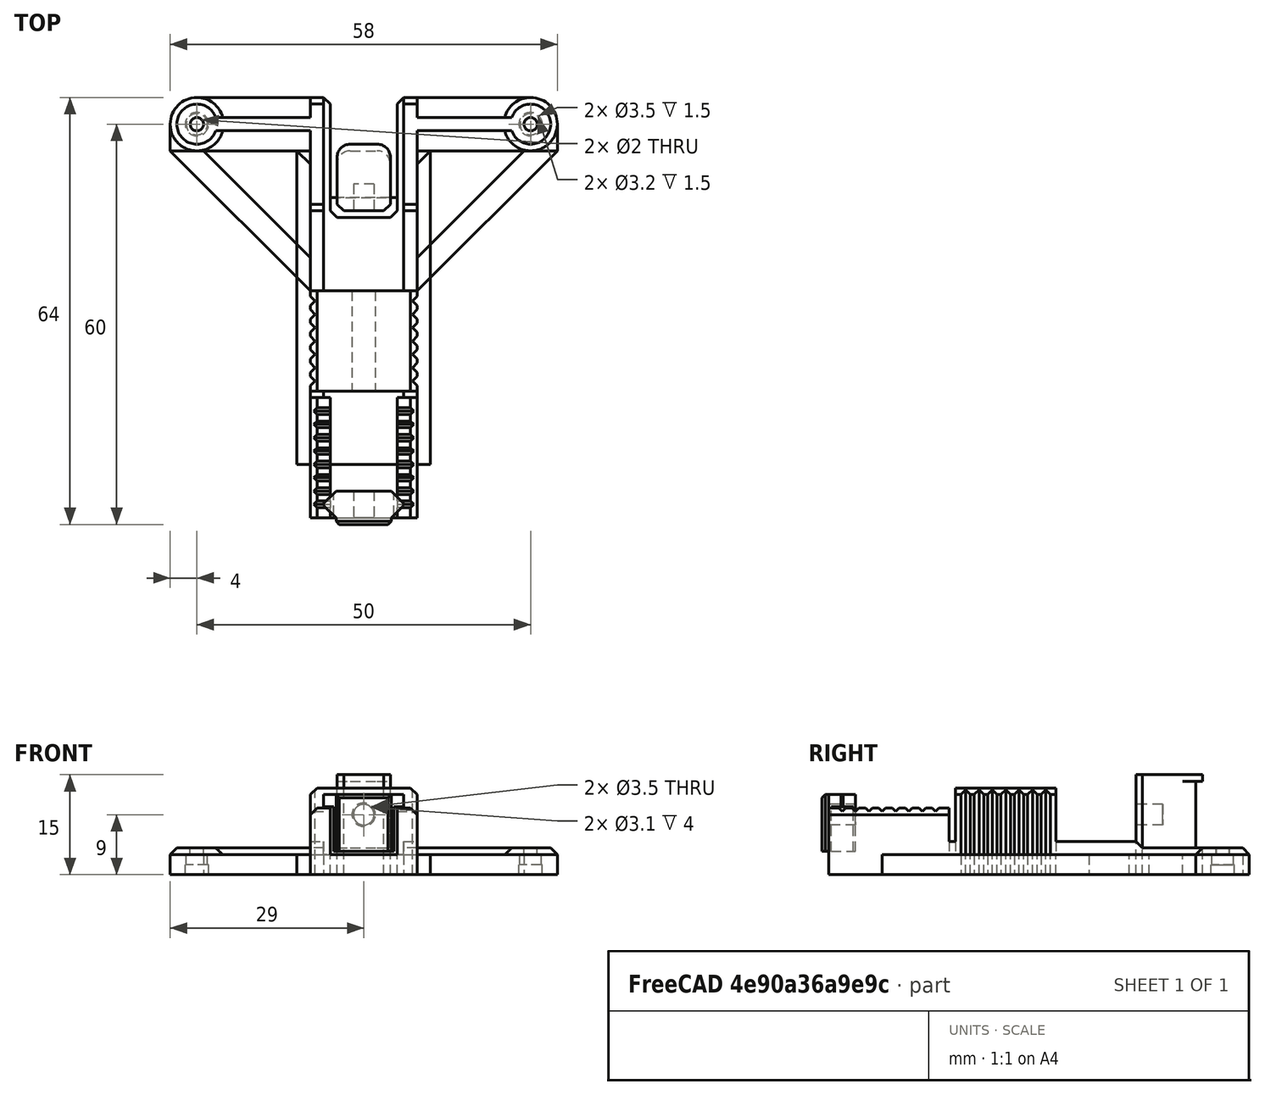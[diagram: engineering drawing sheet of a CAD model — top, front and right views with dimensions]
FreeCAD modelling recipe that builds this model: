
FCSTD DOCUMENT  (FreeCAD 0.18R16146 (Git))
Label: belt-tesioner
License: All rights reserved
LicenseURL: http://en.wikipedia.org/wiki/All_rights_reserved
objects: Part::Chamfer×21, Part::Box×19, Part::Feature×17, Part::MultiFuse×12, Part::Cylinder×11, Part::Cut×9, Part::Fillet×3
note: 92 computed .brp shape members not serialized (recipe doc carries the construction recipe); baked Part::Feature solids carry a one-line shape summary decoded from their .brp

FEATURE [Part::Box] Box  label="Cube"
  AttacherType = Attacher::AttachEngine3D
  Height = 3
  Length = 58
  Placement = pos=(-29,2,0) rot=(0,0,1;0rad)
  Width = 8
FEATURE [Part::Box] Box001  label="Cube001"
  AttacherType = Attacher::AttachEngine3D
  Height = 3
  Length = 16
  Placement = pos=(-8,-53,0) rot=(0,0,1;0rad)
  Width = 57
FEATURE [Part::Cylinder] Cylinder
  Angle = 360
  AttacherType = Attacher::AttachEngine3D
  Height = 10
  Placement = pos=(-25,6,0) rot=(0,0,1;0rad)
  Radius = 1
FEATURE [Part::Cylinder] Cylinder001
  Angle = 360
  AttacherType = Attacher::AttachEngine3D
  Height = 10
  Placement = pos=(25,6,0) rot=(0,0,1;0rad)
  Radius = 1
FEATURE [Part::Cylinder] Cylinder002
  Angle = 360
  AttacherType = Attacher::AttachEngine3D
  Height = 4
  Placement = pos=(-25,6,0) rot=(0,0,1;0rad)
  Radius = 4
FEATURE [Part::Cylinder] Cylinder003
  Angle = 360
  AttacherType = Attacher::AttachEngine3D
  Height = 4
  Placement = pos=(25,6,0) rot=(0,0,1;0rad)
  Radius = 4
FEATURE [Part::Chamfer] Chamfer
  Base = -> Cylinder002
  Edges = 1 edges r=1: [Edge1]
FEATURE [Part::Chamfer] Chamfer001
  Base = -> Cylinder003
  Edges = 1 edges r=1: [Edge1]
FEATURE [Part::Box] Box002  label="Cube002"
  AttacherType = Attacher::AttachEngine3D
  Height = 13
  Length = 16
  Placement = pos=(-8,-34,0) rot=(0,0,1;0rad)
  Width = 15
FEATURE [Part::Cylinder] Cylinder004
  Angle = 360
  AttacherType = Attacher::AttachEngine3D
  Height = 15
  Placement = pos=(0,-19,9) rot=(1,0,0;1.5708rad)
  Radius = 1.75
FEATURE [Part::Cylinder] Cylinder005
  Angle = 360
  AttacherType = Attacher::AttachEngine3D
  Height = 67
  Placement = pos=(0,2e-16,9) rot=(1,0,0;1.5708rad)
  Radius = 1.55
FEATURE [Part::Box] Box003  label="Cube003"
  AttacherType = Attacher::AttachEngine3D
  Height = 12
  Length = 10
  Placement = pos=(-5,-8,0) rot=(0,0,1;0rad)
  Width = 22
FEATURE [Part::Box] Box004  label="Cube004"
  AttacherType = Attacher::AttachEngine3D
  Height = 15
  Length = 8
  Placement = pos=(-4,-4,0) rot=(0,0,1;0rad)
  Width = 10
FEATURE [Part::Box] Box005  label="Cube005"
  AttacherType = Attacher::AttachEngine3D
  Height = 10
  Length = 3
  Placement = pos=(5,-44,0) rot=(0,0,1;0rad)
  Width = 18
FEATURE [Part::Box] Box006  label="Cube006"
  AttacherType = Attacher::AttachEngine3D
  Height = 10
  Length = 3
  Placement = pos=(-8,-44,0) rot=(0,0,1;0rad)
  Width = 18
FEATURE [Part::Box] Box007  label="Cube007"
  AttacherType = Attacher::AttachEngine3D
  Height = 7
  Length = 9
  Placement = pos=(-4.5,-41,3.5) rot=(0,0,1;0rad)
  Width = 4
FEATURE [Part::Box] Box008  label="Cube008"
  AttacherType = Attacher::AttachEngine3D
  Height = 1.8
  Length = 12
  Placement = pos=(-6,-41,10.2) rot=(0,0,1;0rad)
  Width = 4
FEATURE [Part::Chamfer] Chamfer003
  Base = -> Box006
  Edges = 1 edges r=1: [Edge2]
FEATURE [Part::Chamfer] Chamfer004
  Base = -> Box005
  Edges = 1 edges r=1: [Edge6]
FEATURE [Part::Chamfer] Chamfer005
  Edges = 2 edges r=1: [Edge17,Edge36]
FEATURE [Part::Chamfer] Chamfer006
  Base = -> Box008
  Edges = 4 edges r=1.85: [Edge1,Edge3,Edge5,Edge7]
FEATURE [Part::Chamfer] Chamfer007
  Base = -> Box007
  Edges = 4 edges r=0.35: [Edge1,Edge3,Edge5,Edge7]
FEATURE [Part::Box] Box009  label="Cube009"
  AttacherType = Attacher::AttachEngine3D
  Height = 10
  Length = 8
  Placement = pos=(-4,5,4) rot=(0,0,1;0rad)
  Width = 10
FEATURE [Part::Cut] Cut002
  Base = -> Box004
  Tool = -> Box009
FEATURE [Part::Fillet] Fillet001
  Base = -> Cut002
  Edges = 2 edges r=2: [Edge4,Edge17]
FEATURE [Part::Fillet] Fillet002
  Base = -> Fillet001
  Edges = 4 edges r=2: [Edge4,Edge9,Edge19,Edge30]
FEATURE [Part::Cylinder] Cylinder006
  Angle = 360
  AttacherType = Attacher::AttachEngine3D
  Height = 67
  Placement = pos=(0,2e-16,9) rot=(1,0,0;1.5708rad)
  Radius = 1.55
FEATURE [Part::Cut] Cut003
  Base = -> Fillet002
  Placement = pos=(0,-3,0) rot=(0,0,1;0rad)
  Tool = -> Cylinder006
FEATURE [Part::MultiFuse] Fusion001
  Shapes = -> [Chamfer007,Chamfer006]
FEATURE [Part::Cut] Cut004
  Base = -> Fusion001
  Tool = -> Cylinder005
FEATURE [Part::Box] Box010  label="Cube010"
  AttacherType = Attacher::AttachEngine3D
  Height = 8.5
  Length = 8.3
  Placement = pos=(-4.15,-42,3.5) rot=(0,0,1;0rad)
  Width = 1
FEATURE [Part::Chamfer] Chamfer009
  Base = -> Box010
  Edges = 3 edges r=0.5: [Edge1,Edge5,Edge10]
FEATURE [Part::MultiFuse] Fusion002
  Placement = pos=(0,-12,0) rot=(0,0,1;0rad)
  Shapes = -> [Cut004,Chamfer009]
FEATURE [Part::Cylinder] Cylinder007
  Angle = 360
  AttacherType = Attacher::AttachEngine3D
  Height = 1.5
  Placement = pos=(-25,6,0) rot=(0,0,1;0rad)
  Radius = 1.75
FEATURE [Part::Cylinder] Cylinder008
  Angle = 360
  AttacherType = Attacher::AttachEngine3D
  Height = 1.5
  Placement = pos=(25,6,0) rot=(0,0,1;0rad)
  Radius = 1.75
FEATURE [Part::Feature] Box013001  label="Cube014"
  Placement = pos=(0,-28,9.5) rot=(0,0,1;0rad)
  shape: bbox 40 x 2.828 x 2.828 mm, 6 faces (baked)
FEATURE [Part::Feature] Box013002  label="Cube015"
  Placement = pos=(0,-30,9.5) rot=(0,0,1;0rad)
  shape: bbox 40 x 2.828 x 2.828 mm, 6 faces (baked)
FEATURE [Part::Feature] Box013003  label="Cube016"
  Placement = pos=(0,-32,9.5) rot=(0,0,1;0rad)
  shape: bbox 40 x 2.828 x 2.828 mm, 6 faces (baked)
FEATURE [Part::Feature] Box013004  label="Cube017"
  Placement = pos=(0,-34,9.5) rot=(0,0,1;0rad)
  shape: bbox 40 x 2.828 x 2.828 mm, 6 faces (baked)
FEATURE [Part::Feature] Box013005  label="Cube018"
  Placement = pos=(0,-36,9.5) rot=(0,0,1;0rad)
  shape: bbox 40 x 2.828 x 2.828 mm, 6 faces (baked)
FEATURE [Part::Feature] Box013006  label="Cube019"
  Placement = pos=(0,-38,9.5) rot=(0,0,1;0rad)
  shape: bbox 40 x 2.828 x 2.828 mm, 6 faces (baked)
FEATURE [Part::Feature] Box013007  label="Cube020"
  Placement = pos=(0,-40,9.5) rot=(0,0,1;0rad)
  shape: bbox 40 x 2.828 x 2.828 mm, 6 faces (baked)
FEATURE [Part::Feature] Box013008  label="Cube021"
  Placement = pos=(0,-42,9.5) rot=(0,0,1;0rad)
  shape: bbox 40 x 2.828 x 2.828 mm, 6 faces (baked)
FEATURE [Part::MultiFuse] Fusion007
  Shapes = -> [Box013008,Box013003,Box013002,Box013004,Box013006,Box013007,Box013001,Box013005]
FEATURE [Part::MultiFuse] Fusion008
  Shapes = -> [Chamfer004,Chamfer003]
FEATURE [Part::Cut] Cut005
  Base = -> Fusion008
  Placement = pos=(0,-9,0) rot=(0,0,1;0rad)
  Tool = -> Fusion007
FEATURE [Part::Fillet] Fillet
  Base = -> Box
  Edges = 2 edges r=4: [Edge3,Edge7]
FEATURE [Part::MultiFuse] Fusion
  Shapes = -> [Box001,Fillet]
FEATURE [Part::Cut] Cut
  Base = -> Fusion
  Tool = -> Box003
FEATURE [Part::Chamfer] Chamfer014
  Base = -> Cut
  Edges = 2 edges r=1: [Edge28,Edge34]
FEATURE [Part::Chamfer] Chamfer017
  Base = -> Cut003
  Edges = 2 edges r=1: [Edge6,Edge30]
FEATURE [Part::Box] Box013009  label="Cube022"
  AttacherType = Attacher::AttachEngine3D
  Height = 5
  Length = 2
  Placement = pos=(-8,-36,0) rot=(0,0,1;0rad)
  Width = 31
FEATURE [Part::Box] Box013010  label="Cube023"
  AttacherType = Attacher::AttachEngine3D
  Height = 5
  Length = 2
  Placement = pos=(6,-36,0) rot=(0,0,1;0rad)
  Width = 31
FEATURE [Part::Chamfer] Chamfer019
  Base = -> Box013009
  Edges = 1 edges r=2: [Edge12]
FEATURE [Part::Chamfer] Chamfer020
  Base = -> Box013010
  Edges = 1 edges r=2: [Edge12]
FEATURE [Part::Box] Box013011  label="Cube024"
  AttacherType = Attacher::AttachEngine3D
  Height = 4
  Length = 2
  Placement = pos=(-8,-7,0) rot=(0,0,1;0rad)
  Width = 17
FEATURE [Part::Box] Box013012  label="Cube025"
  AttacherType = Attacher::AttachEngine3D
  Height = 4
  Length = 2
  Placement = pos=(6,-7,0) rot=(0,0,1;0rad)
  Width = 17
FEATURE [Part::Chamfer] Chamfer021
  Base = -> Box013012
  Edges = 1 edges r=1: [Edge12]
FEATURE [Part::Chamfer] Chamfer022
  Base = -> Box013011
  Edges = 1 edges r=1: [Edge12]
FEATURE [Part::Box] Box013013  label="Cube026"
  AttacherType = Attacher::AttachEngine3D
  Height = 4
  Length = 15
  Placement = pos=(-23,5,0) rot=(0,0,1;0rad)
  Width = 2
FEATURE [Part::Box] Box013014  label="Cube027"
  AttacherType = Attacher::AttachEngine3D
  Height = 4
  Length = 15
  Placement = pos=(8,5,0) rot=(0,0,1;0rad)
  Width = 2
FEATURE [Part::Box] Box013015  label="Cube028"
  AttacherType = Attacher::AttachEngine3D
  Height = 3
  Length = 22
  Placement = pos=(-29,-19,0) rot=(0,0,1;0rad)
  Width = 22
FEATURE [Part::MultiFuse] Fusion011
  Shapes = -> [Box013014,Box013013]
FEATURE [Part::Box] Box013016  label="Cube029"
  AttacherType = Attacher::AttachEngine3D
  Height = 3
  Length = 22
  Placement = pos=(7,-19,0) rot=(0,0,1;0rad)
  Width = 22
FEATURE [Part::Chamfer] Chamfer023
  Base = -> Box013015
  Edges = 1 edges r=21: [Edge1]
FEATURE [Part::Chamfer] Chamfer024
  Base = -> Box013016
  Edges = 1 edges r=21: [Edge5]
FEATURE [Part::Chamfer] Chamfer025
  Base = -> Chamfer024
  Edges = 1 edges r=18: [Edge12]
FEATURE [Part::Chamfer] Chamfer026
  Base = -> Chamfer023
  Edges = 1 edges r=18: [Edge12]
FEATURE [Part::MultiFuse] Fusion012
  Shapes = -> [Chamfer025,Chamfer026]
FEATURE [Part::Cut] Cut006
  Base = -> Box002
  Tool = -> Cylinder004
FEATURE [Part::Chamfer] Chamfer027
  Base = -> Cut006
  Edges = 2 edges r=1: [Edge2,Edge10]
FEATURE [Part::Chamfer] Chamfer028
  Base = -> Chamfer014
  Edges = 2 edges r=1: [Edge7,Edge32]
FEATURE [Part::MultiFuse] Fusion013
  Shapes = -> [Chamfer028,Chamfer027,Fusion012,Fusion011,Chamfer,Chamfer001,Cut005,Chamfer020,Chamfer019,Chamfer022,Chamfer021]
FEATURE [Part::Feature] Box013017001  label="Cube031"
  Placement = pos=(-8.75,-20.5,0) rot=(0,0,1;0rad)
  shape: bbox 1.414 x 1.414 x 20 mm, 6 faces (baked)
FEATURE [Part::Feature] Box013017002  label="Cube032"
  Placement = pos=(-8.75,-22.5,0) rot=(0,0,1;0rad)
  shape: bbox 1.414 x 1.414 x 20 mm, 6 faces (baked)
FEATURE [Part::Feature] Box013017003  label="Cube033"
  Placement = pos=(-8.75,-24.5,0) rot=(0,0,1;0rad)
  shape: bbox 1.414 x 1.414 x 20 mm, 6 faces (baked)
FEATURE [Part::Feature] Box013017004  label="Cube034"
  Placement = pos=(-8.75,-26.5,0) rot=(0,0,1;0rad)
  shape: bbox 1.414 x 1.414 x 20 mm, 6 faces (baked)
FEATURE [Part::Feature] Box013017005  label="Cube035"
  Placement = pos=(-8.75,-28.5,0) rot=(0,0,1;0rad)
  shape: bbox 1.414 x 1.414 x 20 mm, 6 faces (baked)
FEATURE [Part::Feature] Box013017006  label="Cube036"
  Placement = pos=(-8.75,-30.5,0) rot=(0,0,1;0rad)
  shape: bbox 1.414 x 1.414 x 20 mm, 6 faces (baked)
FEATURE [Part::Feature] Box013017007  label="Cube037"
  Placement = pos=(-8.75,-32.5,0) rot=(0,0,1;0rad)
  shape: bbox 1.414 x 1.414 x 20 mm, 6 faces (baked)
FEATURE [Part::MultiFuse] Fusion014
  Placement = pos=(0.042,0,0) rot=(0,0,1;0rad)
  Shapes = -> [Box013017007,Box013017006,Box013017005,Box013017004,Box013017003,Box013017002,Box013017001]
FEATURE [Part::Feature] Fusion014001  label="Fusion015"
  Placement = pos=(16.042,0,0) rot=(0,0,1;0rad)
  shape: bbox 1.414 x 13.41 x 20 mm, 42 faces, 7 solids (baked)
FEATURE [Part::MultiFuse] Fusion014002
  Shapes = -> [Fusion014001,Fusion014]
FEATURE [Part::Cylinder] Cylinder009
  Angle = 360
  AttacherType = Attacher::AttachEngine3D
  Height = 3
  Placement = pos=(-25,6,0) rot=(0,0,1;0rad)
  Radius = 1.6
FEATURE [Part::Cylinder] Cylinder010
  Angle = 360
  AttacherType = Attacher::AttachEngine3D
  Height = 3
  Placement = pos=(25,6,0) rot=(0,0,1;0rad)
  Radius = 1.6
FEATURE [Part::MultiFuse] Fusion014003  label="thread-insert"
  Shapes = -> [Cylinder009,Cylinder010,Cylinder007,Cylinder008]
FEATURE [Part::MultiFuse] Fusion014004
  Shapes = -> [Cylinder,Cylinder001]
FEATURE [Part::Cut] Cut007
  Base = -> Fusion013
  Tool = -> Fusion014002
FEATURE [Part::Feature] Cut007001  label="Cut008"
  shape: bbox 58 x 63 x 13 mm, 170 faces (baked)
FEATURE [Part::Chamfer] Chamfer029
  Base = -> Cut007001
  Edges = 2 edges r=2: [Edge430,Edge468]
FEATURE [Part::Cut] Cut007002
  Base = -> Chamfer029
  Tool = -> Fusion014004
FEATURE [Part::Cut] Cut007003
  Base = -> Cut007002
  Tool = -> Fusion014003
